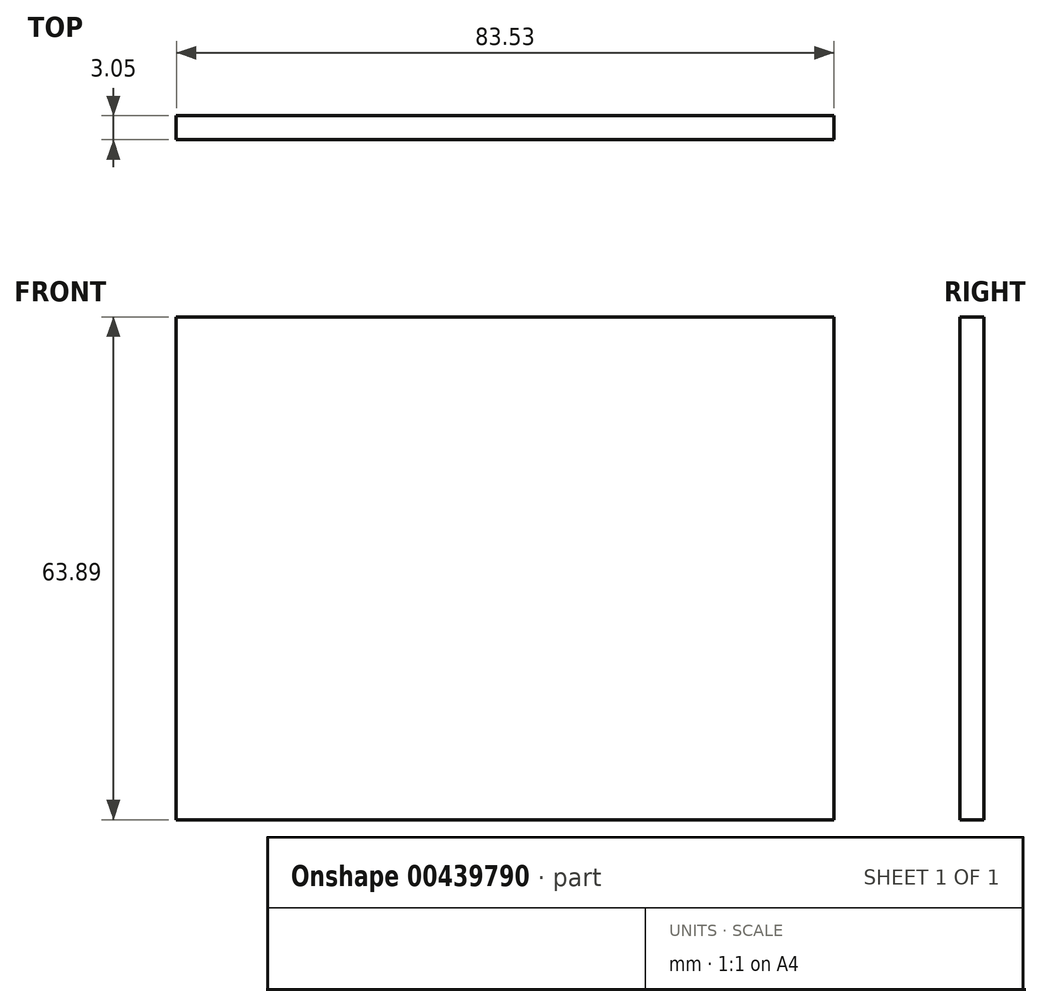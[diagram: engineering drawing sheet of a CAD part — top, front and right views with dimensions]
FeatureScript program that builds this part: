
annotation { "Feature Type Name" : "Feature", "Feature Type Description" : "" }
export const myFeature = defineFeature(function(context is Context, id is Id, definition is map)
    precondition{}
    {
        {
            var Q0;
            Q0=qCreatedBy(makeId("Front.planeOp"),FACE);
            var sketch = newSketch(context, id + "F0", { "sketchPlane" : qUnion([Q0])});
            skLineSegment(sketch, "E0.bottom", {"start": v(-38.04, 21.97) * mm, "end": v(45.49, 21.97) * mm});
            skLineSegment(sketch, "E0.top", {"start": v(-38.04, -41.92) * mm, "end": v(45.49, -41.92) * mm});
            skLineSegment(sketch, "E0.left", {"start": v(-38.04, 21.97) * mm, "end": v(-38.04, -41.92) * mm});
            skLineSegment(sketch, "E0.right", {"start": v(45.49, 21.97) * mm, "end": v(45.49, -41.92) * mm});
            skSolve(sketch);
        }
        {
            var Q0;
            Q0=makeQuery(id+"F0.imprint","IMPRINT",FACE,{"disambiguationData":[TD([[makeQuery(id+"F0.imprint","IMPRINT",EDGE,{"derivedFrom":sQuery(id+"F0.wireOp",EDGE,"E0.bottom")}),-1.0]])]});
            extrude(context, id + "F1", {"entities" : qUnion([Q0]), "depth" : 3.05 * mm});
        }
    });
